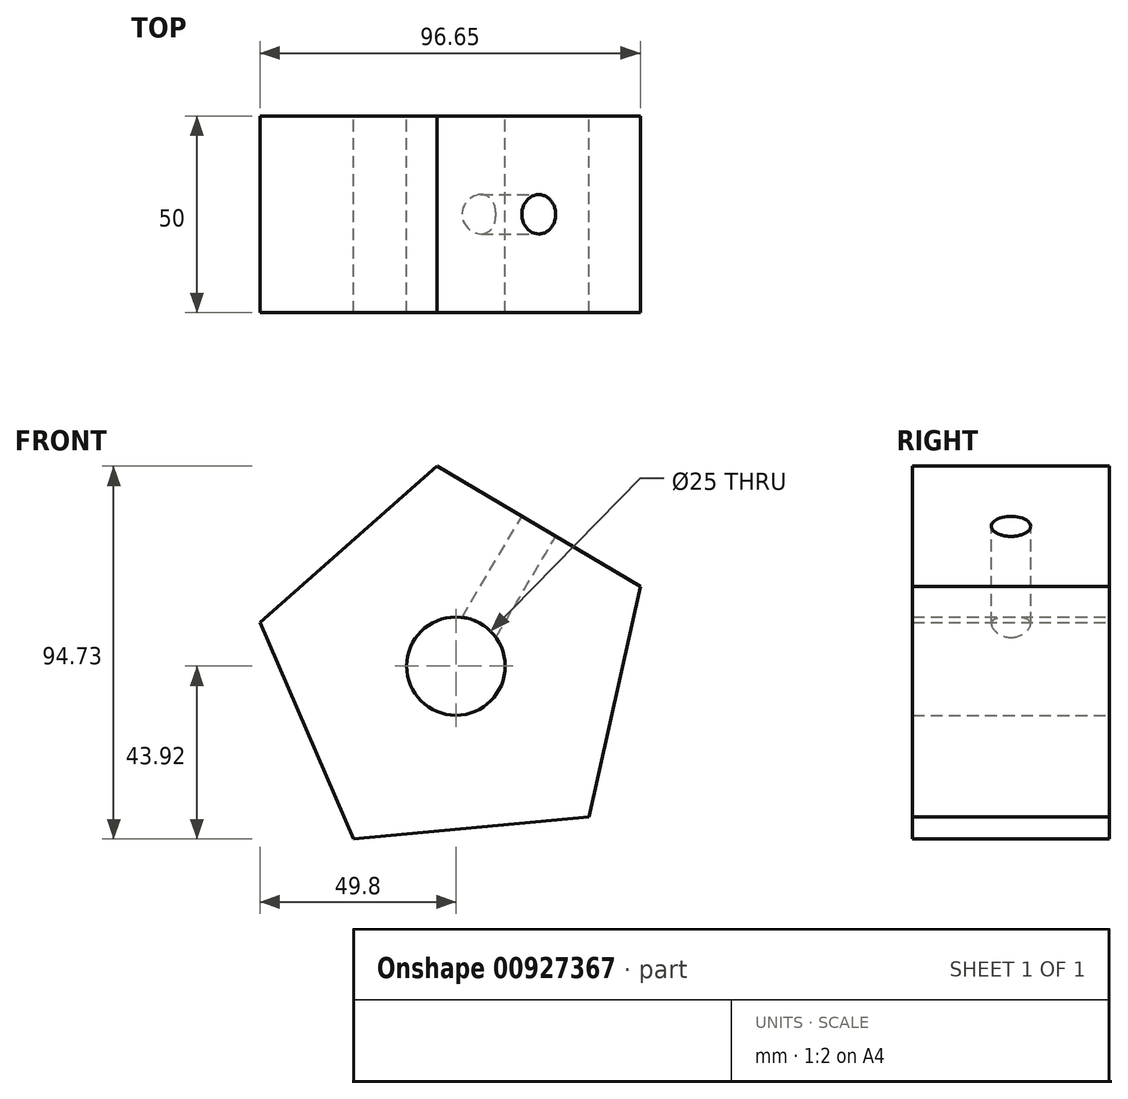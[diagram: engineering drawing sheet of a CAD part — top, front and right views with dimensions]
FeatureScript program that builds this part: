
annotation { "Feature Type Name" : "Feature", "Feature Type Description" : "" }
export const myFeature = defineFeature(function(context is Context, id is Id, definition is map)
    precondition{}
    {
        {
            var Q0;
            Q0=qCreatedBy(makeId("Front.planeOp"),FACE);
            var sketch = newSketch(context, id + "F0", { "sketchPlane" : qUnion([Q0])});
            skCircle(sketch, "E0.cCircle", {"center": v(0, 0) * mm, "radius": 41.3 * mm, "construction": true});
            skLineSegment(sketch, "E0.0", {"start": v(-4.78, 50.81) * mm, "end": v(46.85, 20.25) * mm});
            skLineSegment(sketch, "E0.1", {"start": v(46.85, 20.25) * mm, "end": v(33.73, -38.3) * mm});
            skLineSegment(sketch, "E0.2", {"start": v(33.73, -38.3) * mm, "end": v(-26, -43.92) * mm});
            skLineSegment(sketch, "E0.3", {"start": v(-26, -43.92) * mm, "end": v(-49.8, 11.16) * mm});
            skLineSegment(sketch, "E0.4", {"start": v(-49.8, 11.16) * mm, "end": v(-4.78, 50.81) * mm});
            skPoint(sketch, "E0.0.midPoint", {"position": v(21.04, 35.53) * mm});
            skCircle(sketch, "E1", {"center": v(0, 0) * mm, "radius": 12.5 * mm});
            skPoint(sketch, "E2.center.orphan", {"position": v(0, -20.5) * mm});
            skSolve(sketch);
        }
        {
            var Q0;
            Q0 = qSketchRegion(id + "F0", true);
            extrude(context, id + "F1", {"entities" : qUnion([Q0]), "depth" : 50 * mm, "offsetDistance" : 25 * mm});
        }
        {
            var Q0;
            Q0=makeQuery(id+"F1.opExtrude","SWEPT_FACE",FACE,{"disambiguationData":[OSD([sQuery(id+"F0.wireOp",EDGE,"E0.0")])]});
            var sketch = newSketch(context, id + "F2", { "sketchPlane" : qUnion([Q0])});
            skCircle(sketch, "E3", {"center": v(0, -25) * mm, "radius": 5 * mm});
            skSolve(sketch);
        }
        {
            var Q0;
            Q0 = qSketchRegion(id + "F2", true);
            extrude(context, id + "F3", {"entities" : qUnion([Q0]), "operationType" : NewBodyOperationType.REMOVE, "endBound" : BoundingType.UP_TO_NEXT, "oppositeDirection" : true, "depth" : 25 * mm, "offsetDistance" : 25 * mm});
        }
    });
